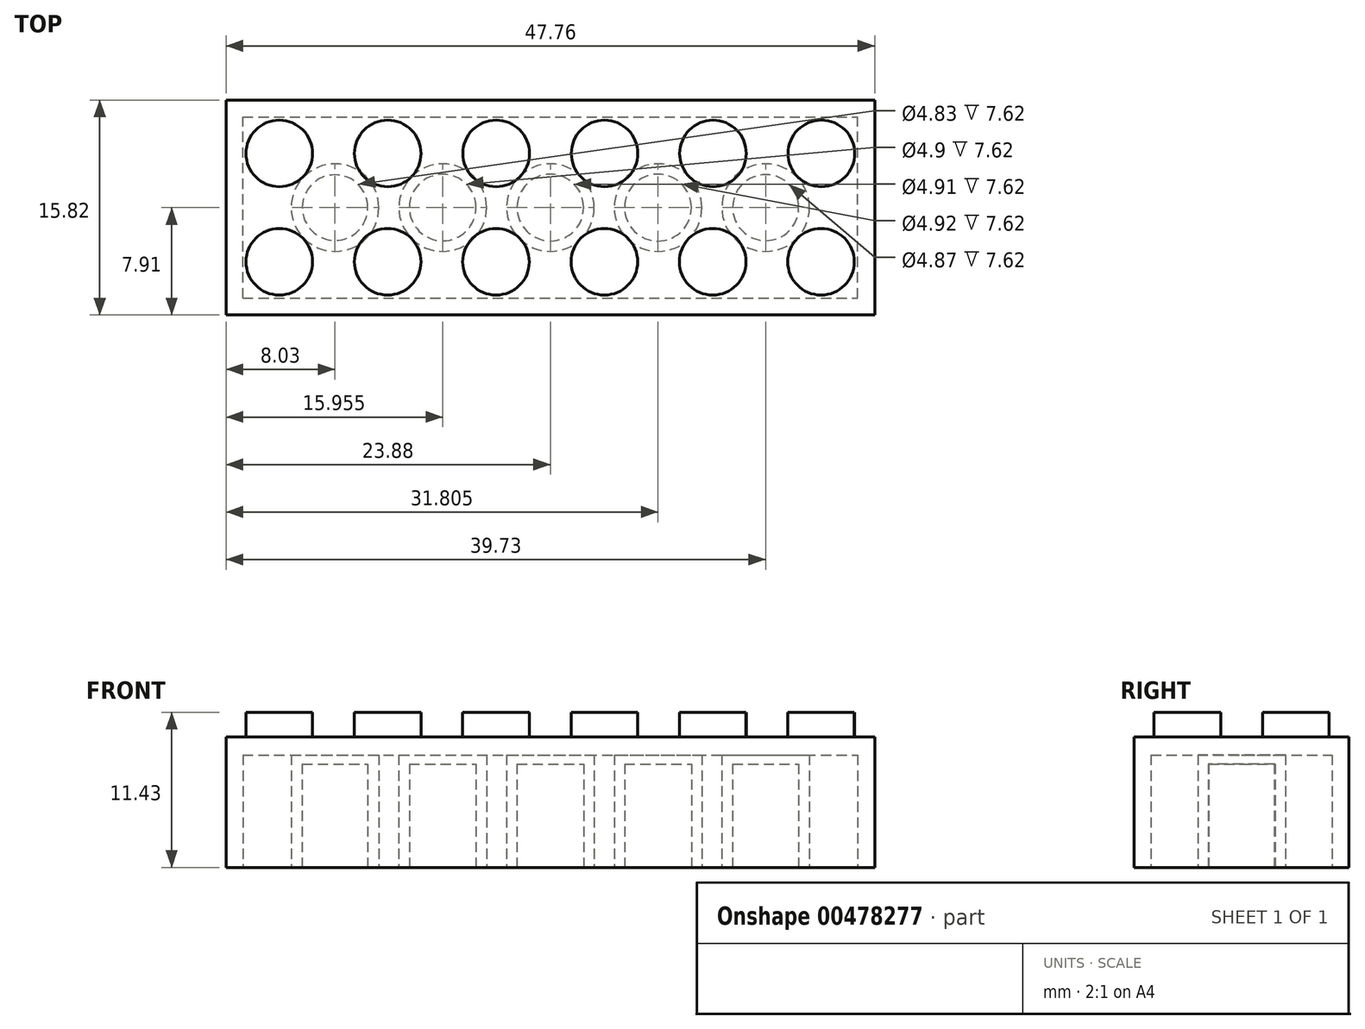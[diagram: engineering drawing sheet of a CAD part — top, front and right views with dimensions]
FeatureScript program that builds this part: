
annotation { "Feature Type Name" : "Feature", "Feature Type Description" : "" }
export const myFeature = defineFeature(function(context is Context, id is Id, definition is map)
    precondition{}
    {
        {
            var Q0;
            Q0=qCreatedBy(makeId("Top.planeOp"),FACE);
            var sketch = newSketch(context, id + "F0", { "sketchPlane" : qUnion([Q0])});
            skLineSegment(sketch, "E0.bottom", {"start": v(-23.88, 7.91) * mm, "end": v(23.88, 7.91) * mm});
            skLineSegment(sketch, "E0.top", {"start": v(-23.88, -7.91) * mm, "end": v(23.88, -7.91) * mm});
            skLineSegment(sketch, "E0.left", {"start": v(-23.88, 7.91) * mm, "end": v(-23.88, -7.91) * mm});
            skLineSegment(sketch, "E0.right", {"start": v(23.88, 7.91) * mm, "end": v(23.88, -7.91) * mm});
            skPoint(sketch, "E0.middle", {"position": v(0, 0) * mm});
            skCircle(sketch, "E1", {"center": v(-19.95, 3.99) * mm, "radius": 2.45 * mm});
            skCircle(sketch, "E2", {"center": v(-19.95, -3.99) * mm, "radius": 2.45 * mm});
            skCircle(sketch, "E3", {"center": v(-11.97, 3.99) * mm, "radius": 2.45 * mm});
            skCircle(sketch, "E4", {"center": v(-4, 3.99) * mm, "radius": 2.45 * mm});
            skCircle(sketch, "E5", {"center": v(4, 3.99) * mm, "radius": 2.45 * mm});
            skCircle(sketch, "E6", {"center": v(11.97, 3.99) * mm, "radius": 2.45 * mm});
            skCircle(sketch, "E7", {"center": v(19.95, 3.99) * mm, "radius": 2.45 * mm});
            skCircle(sketch, "E8", {"center": v(19.93, -3.99) * mm, "radius": 2.45 * mm});
            skCircle(sketch, "E9", {"center": v(11.95, -3.99) * mm, "radius": 2.45 * mm});
            skCircle(sketch, "E10", {"center": v(3.98, -3.99) * mm, "radius": 2.45 * mm});
            skCircle(sketch, "E11", {"center": v(-4, -3.99) * mm, "radius": 2.45 * mm});
            skCircle(sketch, "E12", {"center": v(-11.98, -3.99) * mm, "radius": 2.45 * mm});
            skSolve(sketch);
        }
        {
            var Q0;
            Q0=makeQuery(id+"F0.imprint","IMPRINT",FACE,{"disambiguationData":[TD([[makeQuery(id+"F0.imprint","IMPRINT",EDGE,{"derivedFrom":sQuery(id+"F0.wireOp",EDGE,"E0.bottom")}),-1.0]])]});
            var Q1;
            Q1=makeQuery(id+"F0.imprint","IMPRINT",FACE,{"disambiguationData":[TD([[makeQuery(id+"F0.imprint","IMPRINT",EDGE,{"derivedFrom":sQuery(id+"F0.wireOp",EDGE,"E1")}),1.0]])]});
            var Q2;
            Q2=makeQuery(id+"F0.imprint","IMPRINT",FACE,{"disambiguationData":[TD([[makeQuery(id+"F0.imprint","IMPRINT",EDGE,{"derivedFrom":sQuery(id+"F0.wireOp",EDGE,"E2")}),1.0]])]});
            var Q3;
            Q3=makeQuery(id+"F0.imprint","IMPRINT",FACE,{"disambiguationData":[TD([[makeQuery(id+"F0.imprint","IMPRINT",EDGE,{"derivedFrom":sQuery(id+"F0.wireOp",EDGE,"E12")}),1.0]])]});
            var Q4;
            Q4=makeQuery(id+"F0.imprint","IMPRINT",FACE,{"disambiguationData":[TD([[makeQuery(id+"F0.imprint","IMPRINT",EDGE,{"derivedFrom":sQuery(id+"F0.wireOp",EDGE,"E3")}),1.0]])]});
            var Q5;
            Q5=makeQuery(id+"F0.imprint","IMPRINT",FACE,{"disambiguationData":[TD([[makeQuery(id+"F0.imprint","IMPRINT",EDGE,{"derivedFrom":sQuery(id+"F0.wireOp",EDGE,"E4")}),1.0]])]});
            var Q6;
            Q6=makeQuery(id+"F0.imprint","IMPRINT",FACE,{"disambiguationData":[TD([[makeQuery(id+"F0.imprint","IMPRINT",EDGE,{"derivedFrom":sQuery(id+"F0.wireOp",EDGE,"E11")}),1.0]])]});
            var Q7;
            Q7=makeQuery(id+"F0.imprint","IMPRINT",FACE,{"disambiguationData":[TD([[makeQuery(id+"F0.imprint","IMPRINT",EDGE,{"derivedFrom":sQuery(id+"F0.wireOp",EDGE,"E10")}),1.0]])]});
            var Q8;
            Q8=makeQuery(id+"F0.imprint","IMPRINT",FACE,{"disambiguationData":[TD([[makeQuery(id+"F0.imprint","IMPRINT",EDGE,{"derivedFrom":sQuery(id+"F0.wireOp",EDGE,"E5")}),1.0]])]});
            var Q9;
            Q9=makeQuery(id+"F0.imprint","IMPRINT",FACE,{"disambiguationData":[TD([[makeQuery(id+"F0.imprint","IMPRINT",EDGE,{"derivedFrom":sQuery(id+"F0.wireOp",EDGE,"E9")}),1.0]])]});
            var Q10;
            Q10=makeQuery(id+"F0.imprint","IMPRINT",FACE,{"disambiguationData":[TD([[makeQuery(id+"F0.imprint","IMPRINT",EDGE,{"derivedFrom":sQuery(id+"F0.wireOp",EDGE,"E6")}),1.0]])]});
            var Q11;
            Q11=makeQuery(id+"F0.imprint","IMPRINT",FACE,{"disambiguationData":[TD([[makeQuery(id+"F0.imprint","IMPRINT",EDGE,{"derivedFrom":sQuery(id+"F0.wireOp",EDGE,"E8")}),1.0]])]});
            var Q12;
            Q12=makeQuery(id+"F0.imprint","IMPRINT",FACE,{"disambiguationData":[TD([[makeQuery(id+"F0.imprint","IMPRINT",EDGE,{"derivedFrom":sQuery(id+"F0.wireOp",EDGE,"E7")}),1.0]])]});
            extrude(context, id + "F1", {"entities" : qUnion([Q0, Q1, Q2, Q3, Q4, Q5, Q6, Q7, Q8, Q9, Q10, Q11, Q12]), "depth" : 9.6 * mm, "offsetDistance" : 25.4 * mm});
        }
        {
            var Q0;
            Q0=makeQuery(id+"F0.imprint","IMPRINT",FACE,{"disambiguationData":[TD([[makeQuery(id+"F0.imprint","IMPRINT",EDGE,{"derivedFrom":sQuery(id+"F0.wireOp",EDGE,"E12")}),1.0]])]});
            var Q1;
            Q1=makeQuery(id+"F0.imprint","IMPRINT",FACE,{"disambiguationData":[TD([[makeQuery(id+"F0.imprint","IMPRINT",EDGE,{"derivedFrom":sQuery(id+"F0.wireOp",EDGE,"E2")}),1.0]])]});
            var Q2;
            Q2=makeQuery(id+"F0.imprint","IMPRINT",FACE,{"disambiguationData":[TD([[makeQuery(id+"F0.imprint","IMPRINT",EDGE,{"derivedFrom":sQuery(id+"F0.wireOp",EDGE,"E11")}),1.0]])]});
            var Q3;
            Q3=makeQuery(id+"F0.imprint","IMPRINT",FACE,{"disambiguationData":[TD([[makeQuery(id+"F0.imprint","IMPRINT",EDGE,{"derivedFrom":sQuery(id+"F0.wireOp",EDGE,"E10")}),1.0]])]});
            var Q4;
            Q4=makeQuery(id+"F0.imprint","IMPRINT",FACE,{"disambiguationData":[TD([[makeQuery(id+"F0.imprint","IMPRINT",EDGE,{"derivedFrom":sQuery(id+"F0.wireOp",EDGE,"E9")}),1.0]])]});
            var Q5;
            Q5=makeQuery(id+"F0.imprint","IMPRINT",FACE,{"disambiguationData":[TD([[makeQuery(id+"F0.imprint","IMPRINT",EDGE,{"derivedFrom":sQuery(id+"F0.wireOp",EDGE,"E8")}),1.0]])]});
            var Q6;
            Q6=makeQuery(id+"F0.imprint","IMPRINT",FACE,{"disambiguationData":[TD([[makeQuery(id+"F0.imprint","IMPRINT",EDGE,{"derivedFrom":sQuery(id+"F0.wireOp",EDGE,"E5")}),1.0]])]});
            var Q7;
            Q7=makeQuery(id+"F0.imprint","IMPRINT",FACE,{"disambiguationData":[TD([[makeQuery(id+"F0.imprint","IMPRINT",EDGE,{"derivedFrom":sQuery(id+"F0.wireOp",EDGE,"E6")}),1.0]])]});
            var Q8;
            Q8=makeQuery(id+"F0.imprint","IMPRINT",FACE,{"disambiguationData":[TD([[makeQuery(id+"F0.imprint","IMPRINT",EDGE,{"derivedFrom":sQuery(id+"F0.wireOp",EDGE,"E7")}),1.0]])]});
            var Q9;
            Q9=makeQuery(id+"F0.imprint","IMPRINT",FACE,{"disambiguationData":[TD([[makeQuery(id+"F0.imprint","IMPRINT",EDGE,{"derivedFrom":sQuery(id+"F0.wireOp",EDGE,"E4")}),1.0]])]});
            var Q10;
            Q10=makeQuery(id+"F0.imprint","IMPRINT",FACE,{"disambiguationData":[TD([[makeQuery(id+"F0.imprint","IMPRINT",EDGE,{"derivedFrom":sQuery(id+"F0.wireOp",EDGE,"E3")}),1.0]])]});
            var Q11;
            Q11=makeQuery(id+"F0.imprint","IMPRINT",FACE,{"disambiguationData":[TD([[makeQuery(id+"F0.imprint","IMPRINT",EDGE,{"derivedFrom":sQuery(id+"F0.wireOp",EDGE,"E1")}),1.0]])]});
            extrude(context, id + "F2", {"entities" : qUnion([Q0, Q1, Q2, Q3, Q4, Q5, Q6, Q7, Q8, Q9, Q10, Q11]), "operationType" : NewBodyOperationType.ADD, "depth" : 11.43 * mm, "offsetDistance" : 25.4 * mm});
        }
        {
            var Q0;
            Q0=makeQuery(id+"F1.opExtrude","CAP_FACE",FACE,{"disambiguationData":[OSD([sQuery(id+"F0.wireOp",EDGE,"E0.bottom"),sQuery(id+"F0.wireOp",EDGE,"E0.top"),sQuery(id+"F0.wireOp",EDGE,"E0.left"),sQuery(id+"F0.wireOp",EDGE,"E0.right")])],"isStart":true});
            var sketch = newSketch(context, id + "F3", { "sketchPlane" : qUnion([Q0])});
            skLineSegment(sketch, "E13.bottom", {"start": v(-22.63, 6.67) * mm, "end": v(22.63, 6.67) * mm});
            skLineSegment(sketch, "E13.top", {"start": v(-22.63, -6.67) * mm, "end": v(22.63, -6.67) * mm});
            skLineSegment(sketch, "E13.left", {"start": v(-22.63, 6.67) * mm, "end": v(-22.63, -6.67) * mm});
            skLineSegment(sketch, "E13.right", {"start": v(22.63, 6.67) * mm, "end": v(22.63, -6.67) * mm});
            skCircle(sketch, "E14", {"center": v(-15.85, 0) * mm, "radius": 3.23 * mm});
            skCircle(sketch, "E15", {"center": v(-7.92, 0) * mm, "radius": 3.23 * mm});
            skCircle(sketch, "E16", {"center": v(0, 0) * mm, "radius": 3.23 * mm});
            skCircle(sketch, "E17", {"center": v(7.92, 0) * mm, "radius": 3.23 * mm});
            skCircle(sketch, "E18", {"center": v(15.85, 0) * mm, "radius": 3.23 * mm});
            skSolve(sketch);
        }
        {
            var Q0;
            Q0=makeQuery(id+"F3.imprint","IMPRINT",FACE,{"disambiguationData":[TD([[makeQuery(id+"F3.imprint","IMPRINT",EDGE,{"derivedFrom":sQuery(id+"F3.wireOp",EDGE,"E13.bottom")}),-1.0]])]});
            extrude(context, id + "F4", {"entities" : qUnion([Q0]), "operationType" : NewBodyOperationType.ADD, "oppositeDirection" : true, "depth" : 7.62 * mm, "offsetDistance" : 25.4 * mm});
        }
        {
            var Q0;
            Q0 = qSketchRegion(id + "F3", true);
            extrude(context, id + "F5", {"entities" : qUnion([Q0]), "operationType" : NewBodyOperationType.REMOVE, "oppositeDirection" : true, "depth" : 8.28 * mm, "offsetDistance" : 25.4 * mm});
        }
        {
            var Q0;
            Q0=makeQuery(id+"F5.boolean.opBoolean","SPLIT",FACE,{"disambiguationData":[TD([makeQuery(id+"F5.opExtrude","SWEPT_FACE",FACE,{"disambiguationData":[OSD([sQuery(id+"F3.wireOp",EDGE,"E14")])]})])],"derivedFrom":makeQuery(id+"F1.opExtrude","CAP_FACE",FACE,{"disambiguationData":[OSD([sQuery(id+"F0.wireOp",EDGE,"E0.bottom"),sQuery(id+"F0.wireOp",EDGE,"E0.top"),sQuery(id+"F0.wireOp",EDGE,"E0.left"),sQuery(id+"F0.wireOp",EDGE,"E0.right")])],"isStart":true})});
            var sketch = newSketch(context, id + "F6", { "sketchPlane" : qUnion([Q0])});
            skCircle(sketch, "E19", {"center": v(-15.85, 0) * mm, "radius": 2.41 * mm});
            skSolve(sketch);
        }
        {
            var Q0;
            Q0=makeQuery(id+"F6.imprint","IMPRINT",FACE,{"disambiguationData":[TD([[makeQuery(id+"F6.imprint","IMPRINT",EDGE,{"derivedFrom":sQuery(id+"F6.wireOp",EDGE,"E19")}),1.0]])]});
            extrude(context, id + "F7", {"entities" : qUnion([Q0]), "operationType" : NewBodyOperationType.REMOVE, "oppositeDirection" : true, "depth" : 7.62 * mm, "offsetDistance" : 25.4 * mm});
        }
        {
            var Q0;
            Q0=makeQuery(id+"F5.boolean.opBoolean","SPLIT",FACE,{"disambiguationData":[TD([makeQuery(id+"F5.opExtrude","SWEPT_FACE",FACE,{"disambiguationData":[OSD([sQuery(id+"F3.wireOp",EDGE,"E15")])]})])],"derivedFrom":makeQuery(id+"F1.opExtrude","CAP_FACE",FACE,{"disambiguationData":[OSD([sQuery(id+"F0.wireOp",EDGE,"E0.bottom"),sQuery(id+"F0.wireOp",EDGE,"E0.top"),sQuery(id+"F0.wireOp",EDGE,"E0.left"),sQuery(id+"F0.wireOp",EDGE,"E0.right")])],"isStart":true})});
            var sketch = newSketch(context, id + "F8", { "sketchPlane" : qUnion([Q0])});
            skCircle(sketch, "E20", {"center": v(-7.92, 0) * mm, "radius": 2.45 * mm});
            skSolve(sketch);
        }
        {
            var Q0;
            Q0=makeQuery(id+"F8.imprint","IMPRINT",FACE,{"disambiguationData":[TD([[makeQuery(id+"F8.imprint","IMPRINT",EDGE,{"derivedFrom":sQuery(id+"F8.wireOp",EDGE,"E20")}),1.0]])]});
            extrude(context, id + "F9", {"entities" : qUnion([Q0]), "operationType" : NewBodyOperationType.REMOVE, "oppositeDirection" : true, "depth" : 7.62 * mm, "offsetDistance" : 25.4 * mm});
        }
        {
            var Q0;
            Q0=makeQuery(id+"F5.boolean.opBoolean","SPLIT",FACE,{"disambiguationData":[TD([makeQuery(id+"F5.opExtrude","SWEPT_FACE",FACE,{"disambiguationData":[OSD([sQuery(id+"F3.wireOp",EDGE,"E16")])]})])],"derivedFrom":makeQuery(id+"F1.opExtrude","CAP_FACE",FACE,{"disambiguationData":[OSD([sQuery(id+"F0.wireOp",EDGE,"E0.bottom"),sQuery(id+"F0.wireOp",EDGE,"E0.top"),sQuery(id+"F0.wireOp",EDGE,"E0.left"),sQuery(id+"F0.wireOp",EDGE,"E0.right")])],"isStart":true})});
            var sketch = newSketch(context, id + "F10", { "sketchPlane" : qUnion([Q0])});
            skCircle(sketch, "E21", {"center": v(0, 0) * mm, "radius": 2.45 * mm});
            skSolve(sketch);
        }
        {
            var Q0;
            Q0=makeQuery(id+"F10.imprint","IMPRINT",FACE,{"disambiguationData":[TD([[makeQuery(id+"F10.imprint","IMPRINT",EDGE,{"derivedFrom":sQuery(id+"F10.wireOp",EDGE,"E21")}),1.0]])]});
            extrude(context, id + "F11", {"entities" : qUnion([Q0]), "operationType" : NewBodyOperationType.REMOVE, "oppositeDirection" : true, "depth" : 7.62 * mm, "offsetDistance" : 25.4 * mm});
        }
        {
            var Q0;
            Q0=makeQuery(id+"F5.boolean.opBoolean","SPLIT",FACE,{"disambiguationData":[TD([makeQuery(id+"F5.opExtrude","SWEPT_FACE",FACE,{"disambiguationData":[OSD([sQuery(id+"F3.wireOp",EDGE,"E17")])]})])],"derivedFrom":makeQuery(id+"F1.opExtrude","CAP_FACE",FACE,{"disambiguationData":[OSD([sQuery(id+"F0.wireOp",EDGE,"E0.bottom"),sQuery(id+"F0.wireOp",EDGE,"E0.top"),sQuery(id+"F0.wireOp",EDGE,"E0.left"),sQuery(id+"F0.wireOp",EDGE,"E0.right")])],"isStart":true})});
            var sketch = newSketch(context, id + "F12", { "sketchPlane" : qUnion([Q0])});
            skCircle(sketch, "E22", {"center": v(7.92, 0) * mm, "radius": 2.46 * mm});
            skSolve(sketch);
        }
        {
            var Q0;
            Q0=makeQuery(id+"F12.imprint","IMPRINT",FACE,{"disambiguationData":[TD([[makeQuery(id+"F12.imprint","IMPRINT",EDGE,{"derivedFrom":sQuery(id+"F12.wireOp",EDGE,"E22")}),1.0]])]});
            extrude(context, id + "F13", {"entities" : qUnion([Q0]), "operationType" : NewBodyOperationType.REMOVE, "oppositeDirection" : true, "depth" : 7.62 * mm, "offsetDistance" : 25.4 * mm});
        }
        {
            var Q0;
            Q0=makeQuery(id+"F5.boolean.opBoolean","SPLIT",FACE,{"disambiguationData":[TD([makeQuery(id+"F5.opExtrude","SWEPT_FACE",FACE,{"disambiguationData":[OSD([sQuery(id+"F3.wireOp",EDGE,"E18")])]})])],"derivedFrom":makeQuery(id+"F1.opExtrude","CAP_FACE",FACE,{"disambiguationData":[OSD([sQuery(id+"F0.wireOp",EDGE,"E0.bottom"),sQuery(id+"F0.wireOp",EDGE,"E0.top"),sQuery(id+"F0.wireOp",EDGE,"E0.left"),sQuery(id+"F0.wireOp",EDGE,"E0.right")])],"isStart":true})});
            var sketch = newSketch(context, id + "F14", { "sketchPlane" : qUnion([Q0])});
            skCircle(sketch, "E23", {"center": v(15.85, 0) * mm, "radius": 2.43 * mm});
            skSolve(sketch);
        }
        {
            var Q0;
            Q0=makeQuery(id+"F14.imprint","IMPRINT",FACE,{"disambiguationData":[TD([[makeQuery(id+"F14.imprint","IMPRINT",EDGE,{"derivedFrom":sQuery(id+"F14.wireOp",EDGE,"E23")}),1.0]])]});
            extrude(context, id + "F15", {"entities" : qUnion([Q0]), "operationType" : NewBodyOperationType.REMOVE, "oppositeDirection" : true, "depth" : 7.62 * mm, "offsetDistance" : 25.4 * mm});
        }
    });
